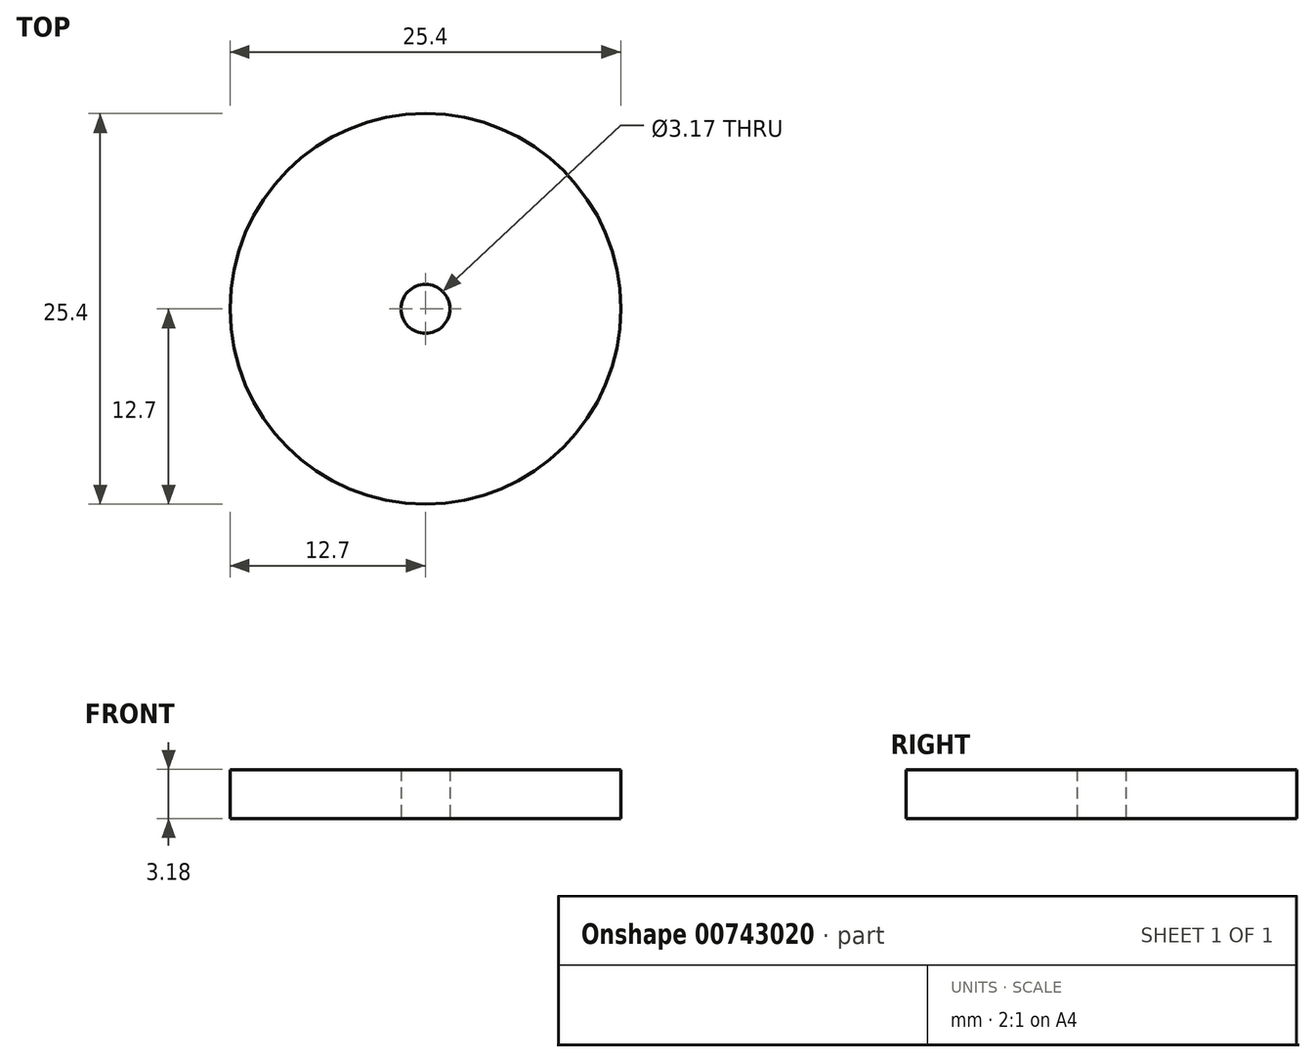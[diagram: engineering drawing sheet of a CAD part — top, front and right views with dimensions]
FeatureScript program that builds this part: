
annotation { "Feature Type Name" : "Feature", "Feature Type Description" : "" }
export const myFeature = defineFeature(function(context is Context, id is Id, definition is map)
    precondition{}
    {
        {
            var Q0;
            Q0=qCreatedBy(makeId("Top.planeOp"),FACE);
            var sketch = newSketch(context, id + "F0", { "sketchPlane" : qUnion([Q0])});
            skCircle(sketch, "E0", {"center": v(0, 0) * mm, "radius": 12.7 * mm});
            skCircle(sketch, "E1", {"center": v(0, 0) * mm, "radius": 1.59 * mm});
            skSolve(sketch);
        }
        {
            var Q0;
            Q0=makeQuery(id+"F0.imprint","IMPRINT",FACE,{"disambiguationData":[TD([[makeQuery(id+"F0.imprint","IMPRINT",EDGE,{"derivedFrom":sQuery(id+"F0.wireOp",EDGE,"E0")}),1.0]])]});
            extrude(context, id + "F1", {"entities" : qUnion([Q0]), "depth" : 3.17 * mm, "offsetDistance" : 25.4 * mm});
        }
    });
